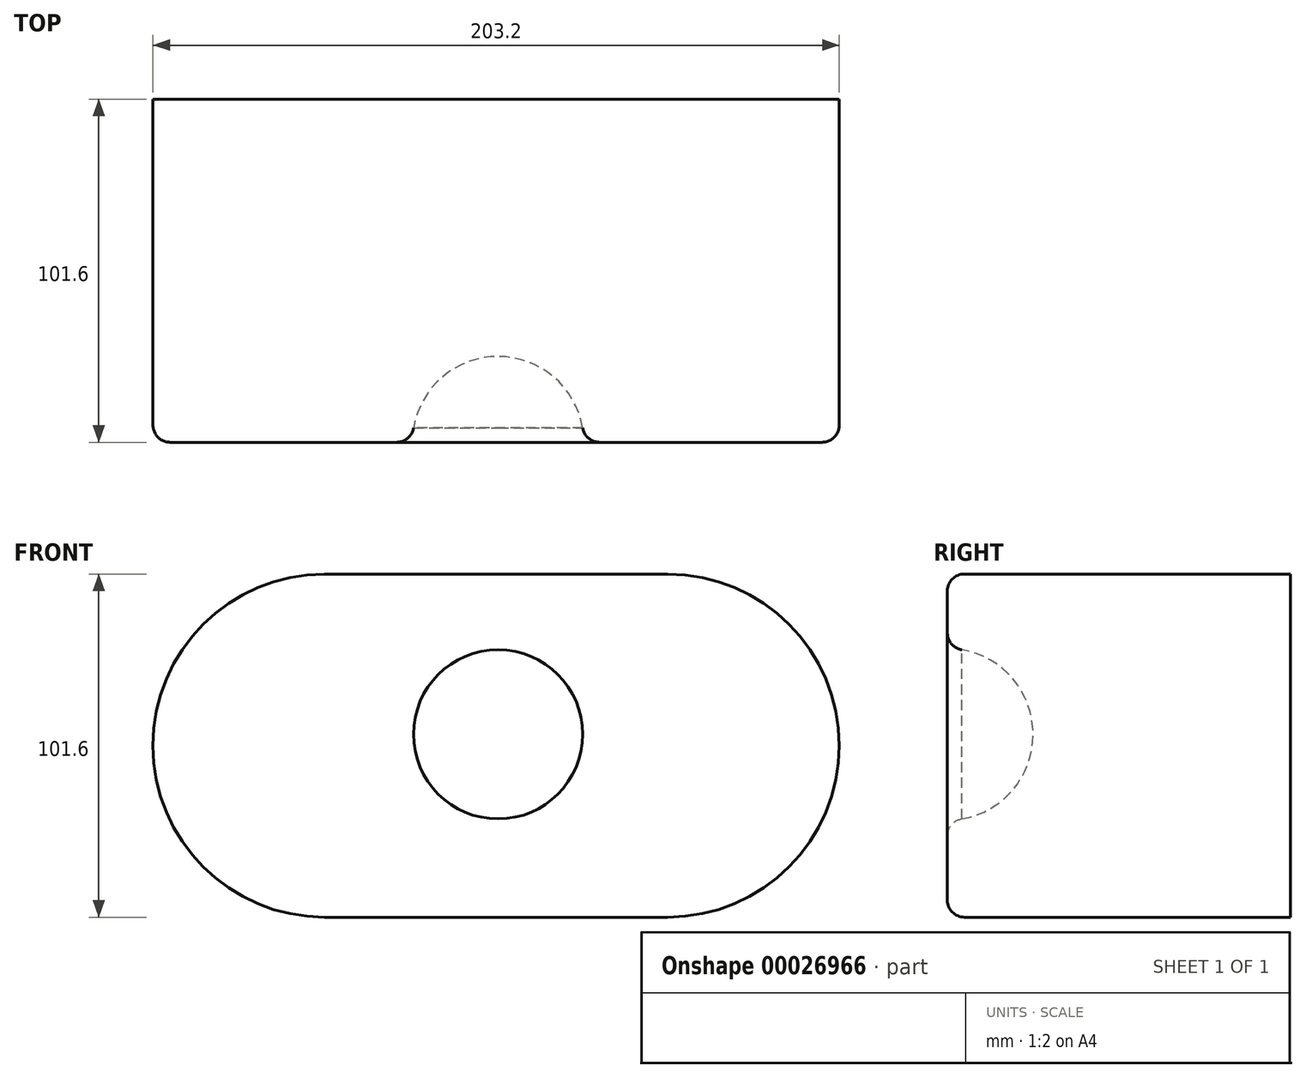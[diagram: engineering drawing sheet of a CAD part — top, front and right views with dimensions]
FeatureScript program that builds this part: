
annotation { "Feature Type Name" : "Feature", "Feature Type Description" : "" }
export const myFeature = defineFeature(function(context is Context, id is Id, definition is map)
    precondition{}
    {
        {
            var Q0;
            Q0=qCreatedBy(makeId("Front.planeOp"),FACE);
            var sketch = newSketch(context, id + "F0", { "sketchPlane" : qUnion([Q0])});
            skLineSegment(sketch, "E0.bottom", {"start": v(-91.77, 74.57) * mm, "end": v(9.83, 74.57) * mm});
            skLineSegment(sketch, "E0.top", {"start": v(-91.77, -27.03) * mm, "end": v(9.83, -27.03) * mm});
            skLineSegment(sketch, "E0.left", {"start": v(-91.77, 74.57) * mm, "end": v(-91.77, -27.03) * mm});
            skLineSegment(sketch, "E0.right", {"start": v(9.83, 74.57) * mm, "end": v(9.83, -27.03) * mm});
            skArc(sketch, "E1", {"start": v(-91.77, 74.57) * mm, "mid": v(-142.57, 23.77) * mm, "end": v(-91.77, -27.03) * mm});
            skArc(sketch, "E2", {"start": v(9.83, -27.03) * mm, "mid": v(60.63, 23.77) * mm, "end": v(9.83, 74.57) * mm});
            skSolve(sketch);
        }
        {
            var Q0;
            Q0=makeQuery(id+"F0.imprint","IMPRINT",FACE,{"disambiguationData":[TD([[makeQuery(id+"F0.imprint","IMPRINT",EDGE,{"derivedFrom":sQuery(id+"F0.wireOp",EDGE,"E0.bottom")}),-1.0]])]});
            var Q1;
            Q1=makeQuery(id+"F0.imprint","IMPRINT",FACE,{"disambiguationData":[TD([[makeQuery(id+"F0.imprint","IMPRINT",EDGE,{"derivedFrom":sQuery(id+"F0.wireOp",EDGE,"E0.left")}),-1.0]])]});
            var Q2;
            Q2=makeQuery(id+"F0.imprint","IMPRINT",FACE,{"disambiguationData":[TD([[makeQuery(id+"F0.imprint","IMPRINT",EDGE,{"derivedFrom":sQuery(id+"F0.wireOp",EDGE,"E0.right")}),1.0]])]});
            extrude(context, id + "F1", {"entities" : qUnion([Q0, Q1, Q2]), "depth" : 101.6 * mm});
        }
        {
            var Q0;
            Q0=makeQuery(id+"F1.opExtrude","CAP_FACE",FACE,{"disambiguationData":[OSD([sQuery(id+"F0.wireOp",EDGE,"E0.bottom"),sQuery(id+"F0.wireOp",EDGE,"E0.top"),sQuery(id+"F0.wireOp",EDGE,"E1"),sQuery(id+"F0.wireOp",EDGE,"E2")])],"isStart":false});
            var sketch = newSketch(context, id + "F2", { "sketchPlane" : qUnion([Q0])});
            skLineSegment(sketch, "E3", {"start": v(-40.38, 52.52) * mm, "end": v(-40.38, 1.72) * mm});
            skArc(sketch, "E4", {"start": v(-40.38, 1.72) * mm, "mid": v(-14.98, 27.12) * mm, "end": v(-40.38, 52.52) * mm});
            skSolve(sketch);
        }
        {
            var Q0;
            Q0=makeQuery(id+"F2.imprint","IMPRINT",FACE,{"disambiguationData":[TD([[makeQuery(id+"F2.imprint","IMPRINT",EDGE,{"derivedFrom":sQuery(id+"F2.wireOp",EDGE,"E3")}),1.0]])]});
            var Q1;
            Q1=sQuery(id+"F2.wireOp",EDGE,"E3");
            revolve(context, id + "F3", {"operationType" : NewBodyOperationType.REMOVE, "entities" : qUnion([Q0]), "axis" : qUnion([Q1]), "revolveType" : RevolveType.FULL, "oppositeDirection" : true});
        }
        {
            var Q0;
            Q0=makeQuery(id+"F1.opExtrude","CAP_EDGE",EDGE,{"disambiguationData":[OSD([sQuery(id+"F0.wireOp",EDGE,"E1")])],"isStart":false});
            var Q1;
            Q1=makeQuery(id+"F1.opExtrude","CAP_FACE",FACE,{"disambiguationData":[OSD([sQuery(id+"F0.wireOp",EDGE,"E0.bottom"),sQuery(id+"F0.wireOp",EDGE,"E0.top"),sQuery(id+"F0.wireOp",EDGE,"E1"),sQuery(id+"F0.wireOp",EDGE,"E2")])],"isStart":false});
            fillet(context, id + "F4", {"entities" : qUnion([Q0, Q1]), "radius" : 5.08 * mm, "tangentPropagation" : true, "allowEdgeOverflow" : false});
        }
    });
